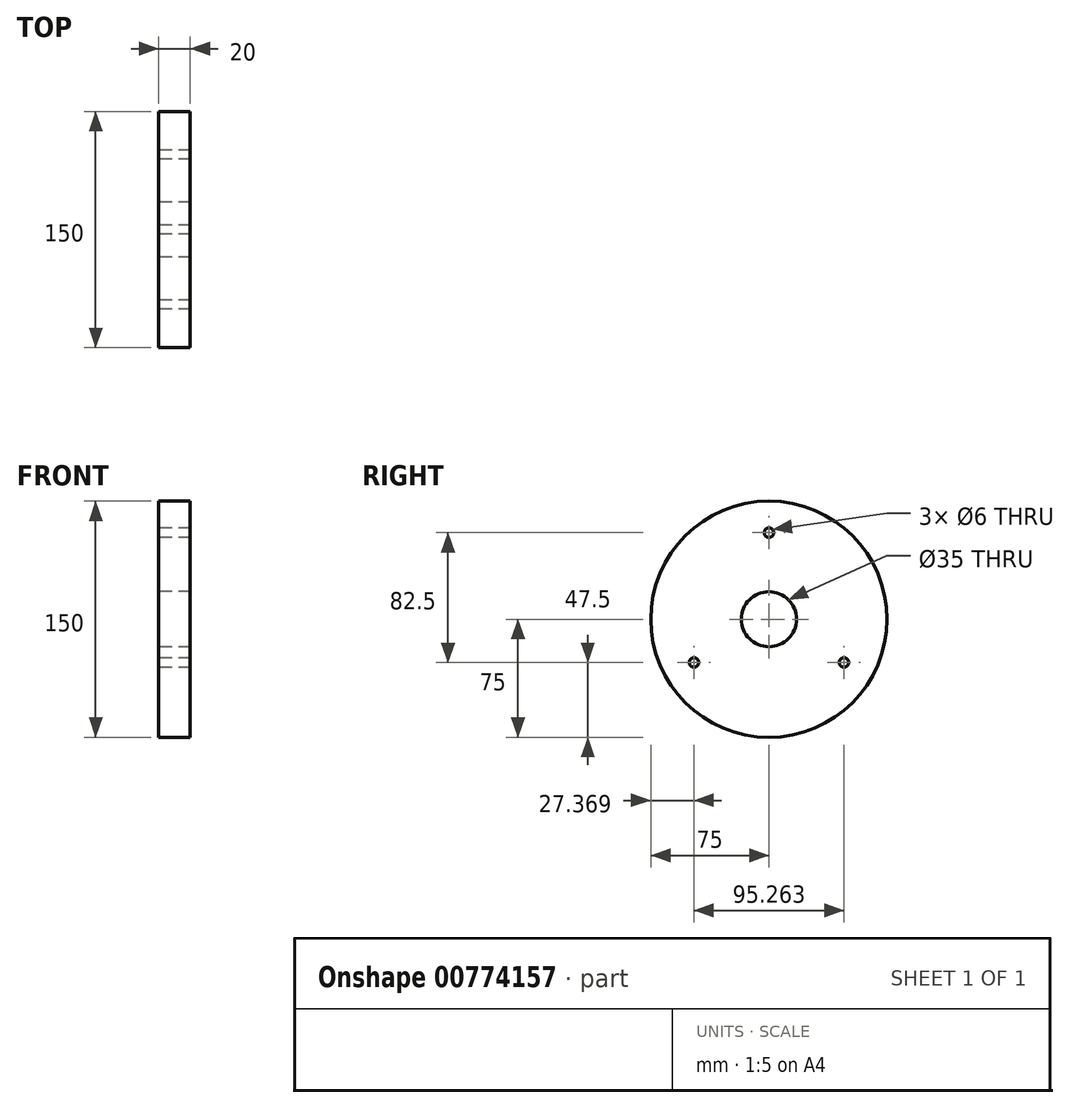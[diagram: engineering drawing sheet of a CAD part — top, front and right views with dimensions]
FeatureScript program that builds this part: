
annotation { "Feature Type Name" : "Feature", "Feature Type Description" : "" }
export const myFeature = defineFeature(function(context is Context, id is Id, definition is map)
    precondition{}
    {
        {
            var Q0;
            Q0=qCreatedBy(makeId("Front.planeOp"),FACE);
            var sketch = newSketch(context, id + "F0", { "sketchPlane" : qUnion([Q0])});
            skLineSegment(sketch, "E0.bottom", {"start": v(0, 0) * mm, "end": v(20, 0) * mm});
            skLineSegment(sketch, "E0.top", {"start": v(0, -75) * mm, "end": v(20, -75) * mm});
            skLineSegment(sketch, "E0.left", {"start": v(0, 0) * mm, "end": v(0, -75) * mm});
            skLineSegment(sketch, "E0.right", {"start": v(20, 0) * mm, "end": v(20, -75) * mm});
            skSolve(sketch);
        }
        {
            var Q0;
            Q0 = qSketchRegion(id + "F0", true);
            var Q1;
            Q1=sQuery(id+"F0.wireOp",EDGE,"E0.bottom");
            revolve(context, id + "F1", {"surfaceOperationType" : NewSurfaceOperationType.NEW, "entities" : qUnion([Q0]), "axis" : qUnion([Q1]), "revolveType" : RevolveType.FULL});
        }
        {
            var Q0;
            Q0=qCreatedBy(makeId("Right.planeOp"),FACE);
            var sketch = newSketch(context, id + "F2", { "sketchPlane" : qUnion([Q0])});
            skCircle(sketch, "E1", {"center": v(0, 0) * mm, "radius": 17.5 * mm});
            skCircle(sketch, "E2", {"center": v(0, 55) * mm, "radius": 3 * mm});
            skCircle(sketch, "E3.1.0", {"center": v(-47.63, -27.5) * mm, "radius": 3 * mm});
            skCircle(sketch, "E3.2.0", {"center": v(47.63, -27.5) * mm, "radius": 3 * mm});
            skSolve(sketch);
        }
        {
            var Q0;
            Q0 = qSketchRegion(id + "F2", true);
            var Q1;
            Q1=makeQuery(id+"F1.opRevolve","SWEPT_FACE",FACE,{"disambiguationData":[OSD([sQuery(id+"F0.wireOp",EDGE,"E0.right")])]});
            extrude(context, id + "F3", {"entities" : qUnion([Q0]), "operationType" : NewBodyOperationType.REMOVE, "endBound" : BoundingType.UP_TO_SURFACE, "depth" : 25 * mm, "endBoundEntityFace" : qUnion([Q1]), "offsetDistance" : 25 * mm});
        }
    });
